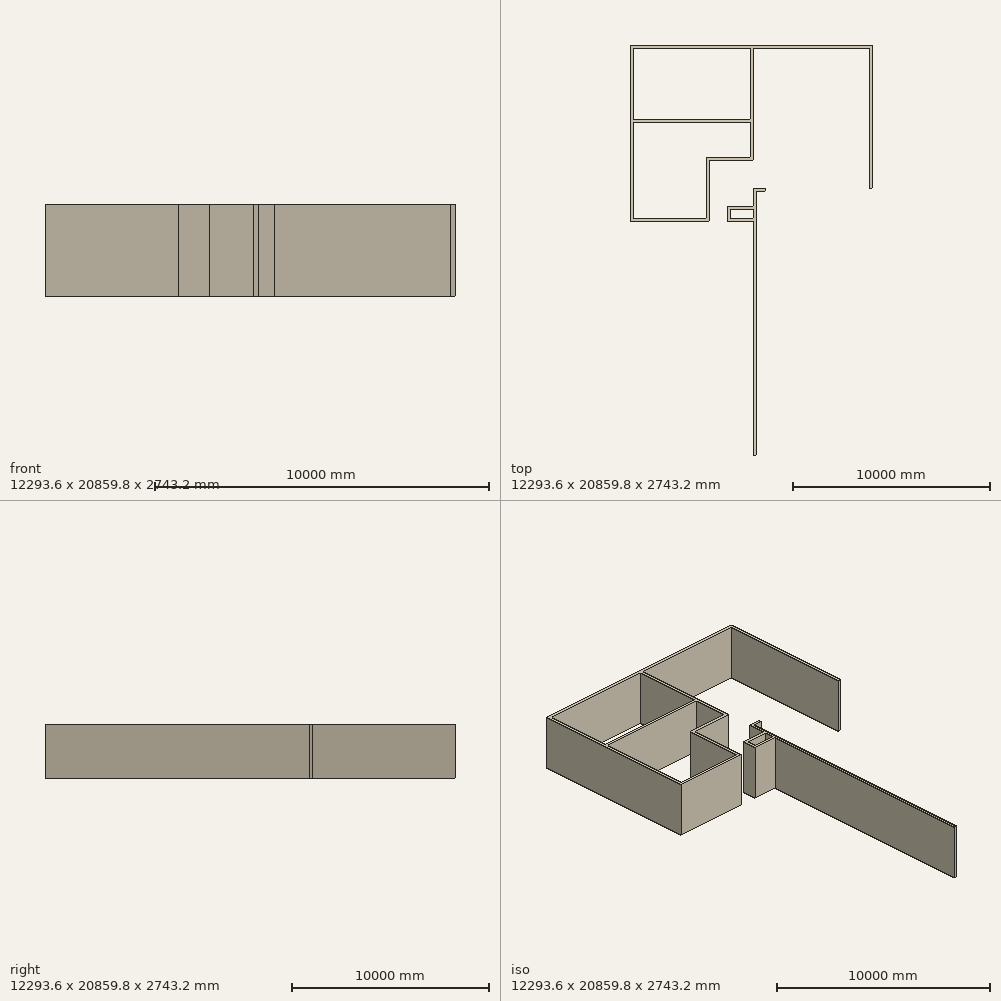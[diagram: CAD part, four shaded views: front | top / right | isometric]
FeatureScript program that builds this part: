
annotation { "Feature Type Name" : "Feature", "Feature Type Description" : "" }
export const myFeature = defineFeature(function(context is Context, id is Id, definition is map)
    precondition{}
    {
        {
            var Q0;
            Q0=qCreatedBy(makeId("Top.planeOp"),FACE);
            var sketch = newSketch(context, id + "F0", { "sketchPlane" : qUnion([Q0])});
            skLineSegment(sketch, "E0.bottom", {"start": v(-3200.4, 3556) * mm, "end": v(3200.4, 3556) * mm});
            skLineSegment(sketch, "E0.top", {"start": v(-3200.4, 0) * mm, "end": v(3200.4, 0) * mm});
            skLineSegment(sketch, "E0.left", {"start": v(-3200.4, 3556) * mm, "end": v(-3200.4, 0) * mm});
            skLineSegment(sketch, "E0.right", {"start": v(3200.4, 3556) * mm, "end": v(3200.4, 0) * mm});
            skLineSegment(sketch, "E1", {"start": v(-3200.4, 3556) * mm, "end": v(-3200.4, 11912.6) * mm});
            skLineSegment(sketch, "E2", {"start": v(-3200.4, 11912.6) * mm, "end": v(787.4, 11912.6) * mm});
            skLineSegment(sketch, "E3", {"start": v(787.4, 11912.6) * mm, "end": v(787.4, 14986) * mm});
            skLineSegment(sketch, "E4", {"start": v(787.4, 14986) * mm, "end": v(3200.4, 14986) * mm});
            skLineSegment(sketch, "E5", {"start": v(3200.4, 14986) * mm, "end": v(3200.4, 20707.35) * mm});
            skLineSegment(sketch, "E6", {"start": v(3200.4, 20707.35) * mm, "end": v(9093.2, 20707.35) * mm});
            skLineSegment(sketch, "E7", {"start": v(9093.2, 20707.35) * mm, "end": v(9093.2, 13595.35) * mm});
            skLineSegment(sketch, "E8", {"start": v(9093.2, 13595.35) * mm, "end": v(3200.4, 13595.35) * mm});
            skLineSegment(sketch, "E9", {"start": v(3200.4, 13595.35) * mm, "end": v(3200.4, 3556) * mm});
            skLineSegment(sketch, "E10", {"start": v(-3200.4, 7112) * mm, "end": v(660.4, 7112) * mm});
            skLineSegment(sketch, "E11", {"start": v(660.4, 11912.6) * mm, "end": v(660.4, 3556) * mm});
            skLineSegment(sketch, "E12", {"start": v(3200.4, 7950.2) * mm, "end": v(660.4, 7950.2) * mm});
            skLineSegment(sketch, "E13", {"start": v(3200.4, 11912.6) * mm, "end": v(1879.6, 11912.6) * mm});
            skLineSegment(sketch, "E14", {"start": v(1879.6, 11912.6) * mm, "end": v(1879.6, 12674.6) * mm});
            skLineSegment(sketch, "E15", {"start": v(1879.6, 12674.6) * mm, "end": v(3200.4, 12674.6) * mm});
            skLineSegment(sketch, "E16", {"start": v(787.4, 14338.3) * mm, "end": v(1612.9, 14338.3) * mm});
            skLineSegment(sketch, "E17", {"start": v(1612.9, 14338.3) * mm, "end": v(1612.9, 14986) * mm});
            skLineSegment(sketch, "E18", {"start": v(1612.9, 14516.1) * mm, "end": v(3200.4, 14516.1) * mm});
            skLineSegment(sketch, "E19", {"start": v(3200.4, 14516.1) * mm, "end": v(3200.4, 14986) * mm});
            skLineSegment(sketch, "E20", {"start": v(3200.4, 14408.15) * mm, "end": v(3200.4, 13595.35) * mm});
            skLineSegment(sketch, "E21.bottom", {"start": v(1676.4, 16205.2) * mm, "end": v(2590.8, 16205.2) * mm});
            skLineSegment(sketch, "E21.top", {"start": v(1676.4, 15290.8) * mm, "end": v(2590.8, 15290.8) * mm});
            skLineSegment(sketch, "E21.left", {"start": v(1676.4, 16205.2) * mm, "end": v(1676.4, 15290.8) * mm});
            skLineSegment(sketch, "E21.right", {"start": v(2590.8, 16205.2) * mm, "end": v(2590.8, 15290.8) * mm});
            skSolve(sketch);
        }
        {
            var Q0;
            Q0=qCreatedBy(makeId("Top.planeOp"),FACE);
            var sketch = newSketch(context, id + "F1", { "sketchPlane" : qUnion([Q0])});
            skLineSegment(sketch, "E22.top", {"start": v(3048, 14986) * mm, "end": v(3200.4, 14986) * mm});
            skLineSegment(sketch, "E22.left", {"start": v(3048, 20707.35) * mm, "end": v(3048, 15138.4) * mm});
            skLineSegment(sketch, "E22.right", {"start": v(3200.4, 20707.35) * mm, "end": v(3200.4, 14986) * mm});
            skLineSegment(sketch, "E23.bottom", {"start": v(3200.4, 20707.35) * mm, "end": v(9093.2, 20707.35) * mm});
            skLineSegment(sketch, "E23.top", {"start": v(3048, 20859.75) * mm, "end": v(9245.6, 20859.75) * mm});
            skLineSegment(sketch, "E23.left", {"start": v(3048, 20859.75) * mm, "end": v(3048, 20707.35) * mm});
            skLineSegment(sketch, "E24.top", {"start": v(9093.2, 13595.35) * mm, "end": v(9245.6, 13595.35) * mm});
            skLineSegment(sketch, "E24.left", {"start": v(9093.2, 20707.35) * mm, "end": v(9093.2, 13595.35) * mm});
            skLineSegment(sketch, "E24.right", {"start": v(9245.6, 20859.75) * mm, "end": v(9245.6, 13595.35) * mm});
            skLineSegment(sketch, "E25.bottom", {"start": v(787.4, 15138.4) * mm, "end": v(3048, 15138.4) * mm});
            skLineSegment(sketch, "E25.top", {"start": v(939.8, 14986) * mm, "end": v(3200.4, 14986) * mm});
            skLineSegment(sketch, "E25.left", {"start": v(787.4, 15138.4) * mm, "end": v(787.4, 14986) * mm});
            skLineSegment(sketch, "E25.right", {"start": v(3200.4, 15138.4) * mm, "end": v(3200.4, 14986) * mm});
            skLineSegment(sketch, "E26.bottom", {"start": v(787.4, 15138.4) * mm, "end": v(939.8, 15138.4) * mm});
            skLineSegment(sketch, "E26.top", {"start": v(787.4, 11912.6) * mm, "end": v(939.8, 11912.6) * mm});
            skLineSegment(sketch, "E26.left", {"start": v(787.4, 15138.4) * mm, "end": v(787.4, 11912.6) * mm});
            skLineSegment(sketch, "E26.right", {"start": v(939.8, 14986) * mm, "end": v(939.8, 11912.6) * mm});
            skLineSegment(sketch, "E27.bottom", {"start": v(3200.4, 13595.35) * mm, "end": v(3352.8, 13595.35) * mm});
            skLineSegment(sketch, "E27.top", {"start": v(3200.4, 0) * mm, "end": v(3352.8, 0) * mm});
            skLineSegment(sketch, "E27.left", {"start": v(3200.4, 13595.35) * mm, "end": v(3200.4, 0) * mm});
            skLineSegment(sketch, "E27.right", {"start": v(3352.8, 13442.95) * mm, "end": v(3352.8, 0) * mm});
            skLineSegment(sketch, "E28.bottom", {"start": v(3352.8, 13595.35) * mm, "end": v(3810, 13595.35) * mm});
            skLineSegment(sketch, "E28.top", {"start": v(3352.8, 13442.95) * mm, "end": v(3810, 13442.95) * mm});
            skLineSegment(sketch, "E28.right", {"start": v(3810, 13595.35) * mm, "end": v(3810, 13442.95) * mm});
            skLineSegment(sketch, "E29.bottom", {"start": v(9245.6, 13595.35) * mm, "end": v(8788.4, 13595.35) * mm});
            skLineSegment(sketch, "E29.top", {"start": v(9245.6, 13442.95) * mm, "end": v(8788.4, 13442.95) * mm});
            skLineSegment(sketch, "E29.left", {"start": v(9245.6, 13595.35) * mm, "end": v(9245.6, 13442.95) * mm});
            skLineSegment(sketch, "E29.right", {"start": v(8788.4, 13595.35) * mm, "end": v(8788.4, 13442.95) * mm});
            skLineSegment(sketch, "E30.bottom", {"start": v(3200.4, 12674.6) * mm, "end": v(1879.6, 12674.6) * mm});
            skLineSegment(sketch, "E30.top", {"start": v(3200.4, 12522.2) * mm, "end": v(1879.6, 12522.2) * mm});
            skLineSegment(sketch, "E30.left", {"start": v(3200.4, 12674.6) * mm, "end": v(3200.4, 12522.2) * mm});
            skLineSegment(sketch, "E30.right", {"start": v(1879.6, 12674.6) * mm, "end": v(1879.6, 12522.2) * mm});
            skLineSegment(sketch, "E31.bottom", {"start": v(1879.6, 11912.6) * mm, "end": v(2032, 11912.6) * mm});
            skLineSegment(sketch, "E31.top", {"start": v(1879.6, 12522.2) * mm, "end": v(2032, 12522.2) * mm});
            skLineSegment(sketch, "E31.left", {"start": v(1879.6, 11912.6) * mm, "end": v(1879.6, 12522.2) * mm});
            skLineSegment(sketch, "E31.right", {"start": v(2032, 11912.6) * mm, "end": v(2032, 12522.2) * mm});
            skLineSegment(sketch, "E32.bottom", {"start": v(2032, 11912.6) * mm, "end": v(3200.4, 11912.6) * mm});
            skLineSegment(sketch, "E32.top", {"start": v(2032, 12065) * mm, "end": v(3200.4, 12065) * mm});
            skLineSegment(sketch, "E32.left", {"start": v(2032, 11912.6) * mm, "end": v(2032, 12065) * mm});
            skLineSegment(sketch, "E32.right", {"start": v(3200.4, 11912.6) * mm, "end": v(3200.4, 12065) * mm});
            skSolve(sketch);
        }
        {
            var Q0;
            Q0=makeQuery(id+"F1.imprint","IMPRINT",FACE,{"disambiguationData":[TD([[makeQuery(id+"F1.imprint","IMPRINT",EDGE,{"derivedFrom":sQuery(id+"F1.wireOp",EDGE,"E22.left")}),1.0]])]});
            var Q1;
            Q1=makeQuery(id+"F1.imprint","IMPRINT",FACE,{"disambiguationData":[TD([[makeQuery(id+"F1.imprint","IMPRINT",EDGE,{"derivedFrom":sQuery(id+"F1.wireOp",EDGE,"E27.bottom")}),-1.0]])]});
            var Q2;
            Q2=makeQuery(id+"F1.imprint","IMPRINT",FACE,{"disambiguationData":[TD([[makeQuery(id+"F1.imprint","IMPRINT",EDGE,{"derivedFrom":sQuery(id+"F1.wireOp",EDGE,"E30.bottom")}),1.0]])]});
            var Q3;
            Q3=makeQuery(id+"F1.imprint","IMPRINT",FACE,{"disambiguationData":[TD([[makeQuery(id+"F1.imprint","IMPRINT",EDGE,{"derivedFrom":sQuery(id+"F1.wireOp",EDGE,"E31.bottom")}),1.0]])]});
            var Q4;
            Q4=makeQuery(id+"F1.imprint","IMPRINT",FACE,{"disambiguationData":[TD([[makeQuery(id+"F1.imprint","IMPRINT",EDGE,{"derivedFrom":sQuery(id+"F1.wireOp",EDGE,"E32.bottom")}),1.0]])]});
            extrude(context, id + "F2", {"entities" : qUnion([Q0, Q1, Q2, Q3, Q4]), "depth" : 2743.2 * mm, "offsetDistance" : 25.4 * mm});
        }
        {
            var Q0;
            Q0=qCreatedBy(makeId("Top.planeOp"),FACE);
            var sketch = newSketch(context, id + "F3", { "sketchPlane" : qUnion([Q0])});
            skLineSegment(sketch, "E33.bottom", {"start": v(3048, 20859.75) * mm, "end": v(-3048, 20859.75) * mm});
            skLineSegment(sketch, "E33.top", {"start": v(3048, 17119.6) * mm, "end": v(-2895.6, 17119.6) * mm});
            skLineSegment(sketch, "E33.left", {"start": v(3048, 20859.75) * mm, "end": v(3048, 17119.6) * mm});
            skLineSegment(sketch, "E33.right", {"start": v(-3048, 20859.75) * mm, "end": v(-3048, 17119.6) * mm});
            skLineSegment(sketch, "E34", {"start": v(-3048, 17119.6) * mm, "end": v(-3048, 11912.6) * mm});
            skLineSegment(sketch, "E35.0", {"start": v(-2895.6, 16967.2) * mm, "end": v(-2895.6, 12065) * mm});
            skLineSegment(sketch, "E36.0", {"start": v(3048, 16967.2) * mm, "end": v(-2895.6, 16967.2) * mm});
            skLineSegment(sketch, "E37.bottom", {"start": v(-2895.6, 12065) * mm, "end": v(787.4, 12065) * mm});
            skLineSegment(sketch, "E37.top", {"start": v(-3048, 11912.6) * mm, "end": v(787.4, 11912.6) * mm});
            skLineSegment(sketch, "E37.right", {"start": v(787.4, 12065) * mm, "end": v(787.4, 11912.6) * mm});
            skLineSegment(sketch, "E38.bottom", {"start": v(-2093.85, 12107.13) * mm, "end": v(-1484.25, 12107.13) * mm});
            skLineSegment(sketch, "E38.top", {"start": v(-2093.85, 12564.33) * mm, "end": v(-1484.25, 12564.33) * mm});
            skLineSegment(sketch, "E38.left", {"start": v(-2093.85, 12107.13) * mm, "end": v(-2093.85, 12564.33) * mm});
            skLineSegment(sketch, "E38.right", {"start": v(-1484.25, 12107.13) * mm, "end": v(-1484.25, 12564.33) * mm});
            skLineSegment(sketch, "E39.0", {"start": v(-2895.6, 20707.35) * mm, "end": v(-2895.6, 17119.6) * mm});
            skLineSegment(sketch, "E40.0", {"start": v(3048, 20707.35) * mm, "end": v(-2895.6, 20707.35) * mm});
            skLineSegment(sketch, "E41", {"start": v(3048, 17119.6) * mm, "end": v(3048, 16967.2) * mm});
            skSolve(sketch);
        }
        {
            var Q0;
            {var subQ0=sQuery(id+"F3.wireOp",EDGE,"E33.bottom");Q0=makeQuery(id+"F3.imprint","IMPRINT",FACE,{"disambiguationData":[TD([[makeQuery(id+"F3.imprint","IMPRINT",EDGE,{"derivedFrom":subQ0}),1.0]])]});}
            extrude(context, id + "F4", {"entities" : qUnion([Q0]), "operationType" : NewBodyOperationType.ADD, "depth" : 2743.2 * mm, "offsetDistance" : 25.4 * mm});
        }
    });
